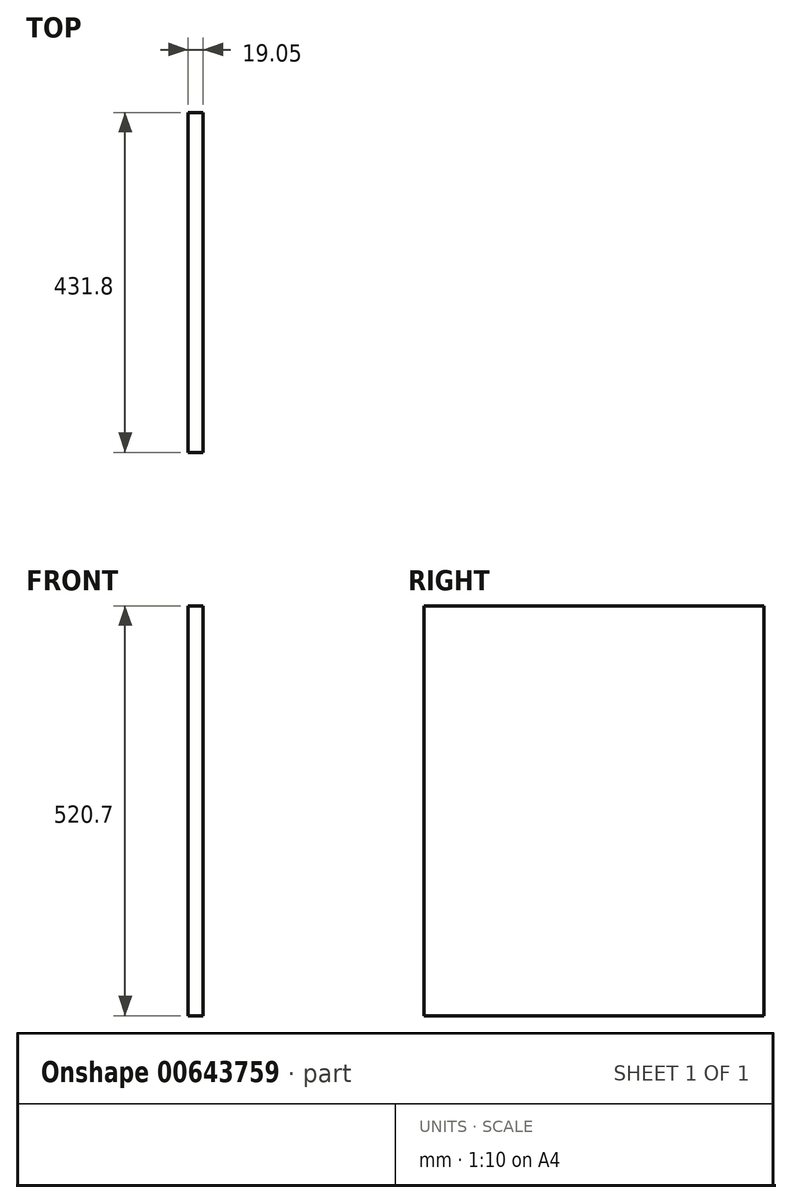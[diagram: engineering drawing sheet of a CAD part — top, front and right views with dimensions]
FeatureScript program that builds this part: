
annotation { "Feature Type Name" : "Feature", "Feature Type Description" : "" }
export const myFeature = defineFeature(function(context is Context, id is Id, definition is map)
    precondition{}
    {
        {
            var Q0;
            Q0=qCreatedBy(makeId("Right.planeOp"),FACE);
            var sketch = newSketch(context, id + "F0", { "sketchPlane" : qUnion([Q0])});
            skLineSegment(sketch, "E0.bottom", {"start": v(0, 0) * mm, "end": v(431.8, 0) * mm});
            skLineSegment(sketch, "E0.top", {"start": v(0, 520.7) * mm, "end": v(431.8, 520.7) * mm});
            skLineSegment(sketch, "E0.left", {"start": v(0, 0) * mm, "end": v(0, 520.7) * mm});
            skLineSegment(sketch, "E0.right", {"start": v(431.8, 0) * mm, "end": v(431.8, 520.7) * mm});
            skSolve(sketch);
        }
        {
            var Q0;
            Q0=makeQuery(id+"F0.imprint","IMPRINT",FACE,{"disambiguationData":[TD([[makeQuery(id+"F0.imprint","IMPRINT",EDGE,{"derivedFrom":sQuery(id+"F0.wireOp",EDGE,"E0.bottom")}),1.0]])]});
            extrude(context, id + "F1", {"entities" : qUnion([Q0]), "depth" : 19.05 * mm, "offsetDistance" : 25.4 * mm});
        }
    });
